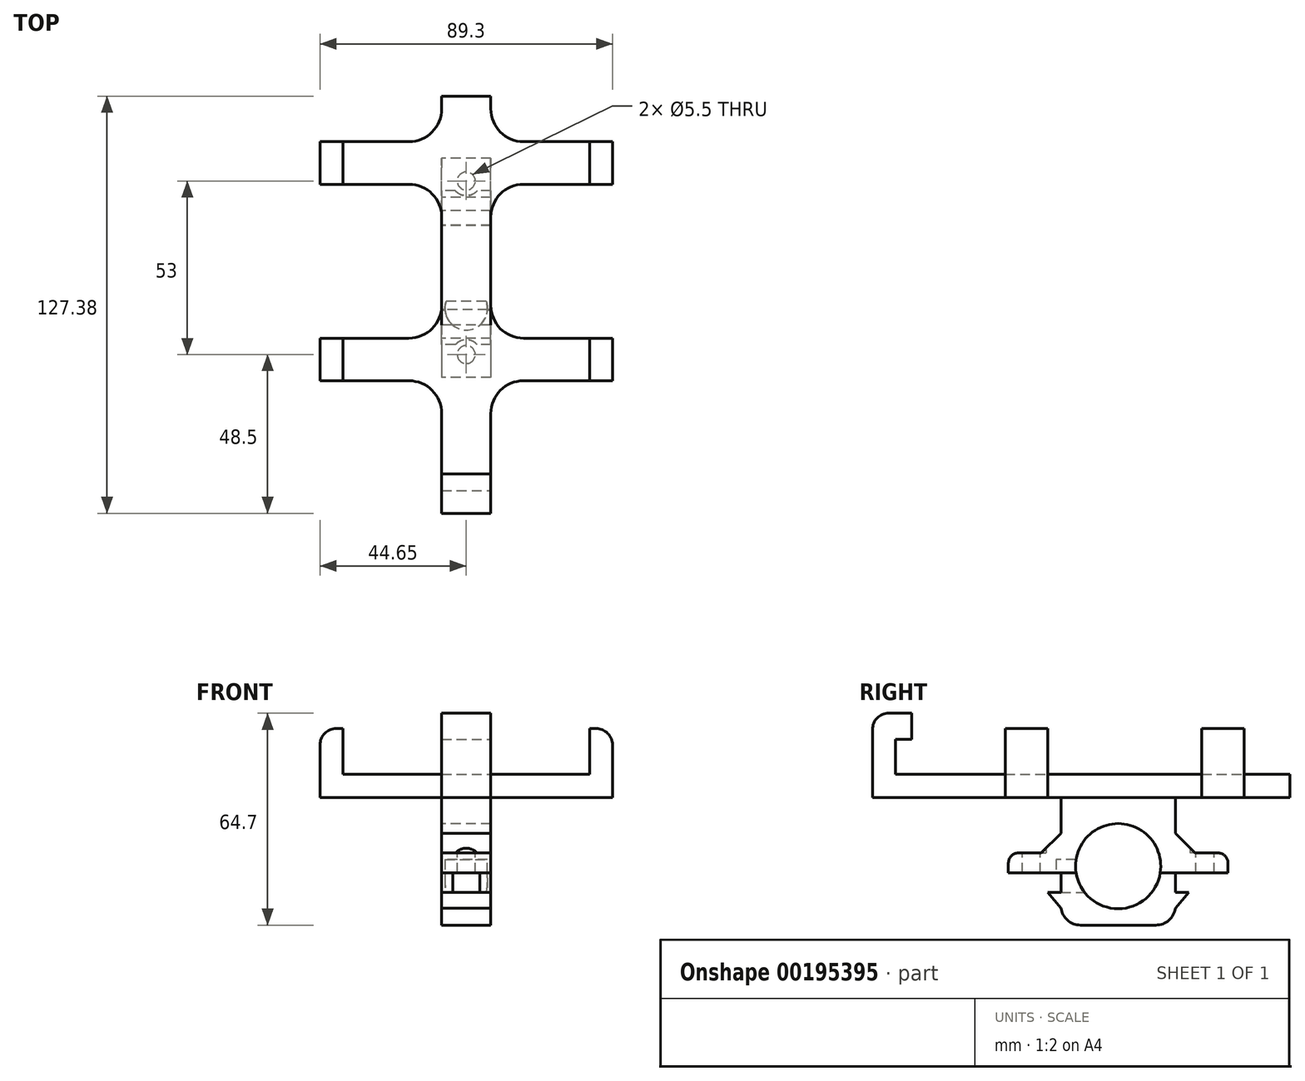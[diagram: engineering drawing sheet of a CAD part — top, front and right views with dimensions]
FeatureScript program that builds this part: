
annotation { "Feature Type Name" : "Feature", "Feature Type Description" : "" }
export const myFeature = defineFeature(function(context is Context, id is Id, definition is map)
    precondition{}
    {
        {
            var Q0;
            Q0=qCreatedBy(makeId("Top.planeOp"),FACE);
            var sketch = newSketch(context, id + "F0", { "sketchPlane" : qUnion([Q0])});
            skPoint(sketch, "E0.middle", {"position": v(0, 0) * mm});
            skPoint(sketch, "E1.middle", {"position": v(0, 25) * mm});
            skPoint(sketch, "E2.middle", {"position": v(0, -35) * mm});
            skLineSegment(sketch, "E3", {"start": v(-7.5, -75) * mm, "end": v(-7.5, 30) * mm});
            skLineSegment(sketch, "E4", {"start": v(7.5, 30) * mm, "end": v(7.5, -75) * mm});
            skLineSegment(sketch, "E5.top", {"start": v(-7.5, 45.38) * mm, "end": v(7.5, 45.38) * mm});
            skLineSegment(sketch, "E5.left", {"start": v(-7.5, 30) * mm, "end": v(-7.5, 45.38) * mm});
            skLineSegment(sketch, "E5.right", {"start": v(7.5, 30) * mm, "end": v(7.5, 45.38) * mm});
            skLineSegment(sketch, "E6.bottom", {"start": v(-37.65, -41.5) * mm, "end": v(37.65, -41.5) * mm});
            skLineSegment(sketch, "E6.top", {"start": v(-37.65, -28.5) * mm, "end": v(37.65, -28.5) * mm});
            skLineSegment(sketch, "E6.left", {"start": v(-37.65, -41.5) * mm, "end": v(-37.65, -28.5) * mm});
            skLineSegment(sketch, "E6.right", {"start": v(37.65, -41.5) * mm, "end": v(37.65, -28.5) * mm});
            skLineSegment(sketch, "E7", {"start": v(-7.5, -75) * mm, "end": v(7.5, -75) * mm});
            skLineSegment(sketch, "E8.bottom", {"start": v(37.65, 18.5) * mm, "end": v(-37.65, 18.5) * mm});
            skLineSegment(sketch, "E8.top", {"start": v(37.65, 31.5) * mm, "end": v(-37.65, 31.5) * mm});
            skLineSegment(sketch, "E8.left", {"start": v(37.65, 18.5) * mm, "end": v(37.65, 31.5) * mm});
            skLineSegment(sketch, "E8.right", {"start": v(-37.65, 18.5) * mm, "end": v(-37.65, 31.5) * mm});
            skLineSegment(sketch, "E9.bottom", {"start": v(-37.65, 31.5) * mm, "end": v(-44.65, 31.5) * mm});
            skLineSegment(sketch, "E9.top", {"start": v(-37.65, 18.5) * mm, "end": v(-44.65, 18.5) * mm});
            skLineSegment(sketch, "E9.left", {"start": v(-37.65, 31.5) * mm, "end": v(-37.65, 18.5) * mm});
            skLineSegment(sketch, "E9.right", {"start": v(-44.65, 31.5) * mm, "end": v(-44.65, 18.5) * mm});
            skLineSegment(sketch, "E10.bottom", {"start": v(-44.65, -28.5) * mm, "end": v(-37.65, -28.5) * mm});
            skLineSegment(sketch, "E10.top", {"start": v(-44.65, -41.5) * mm, "end": v(-37.65, -41.5) * mm});
            skLineSegment(sketch, "E10.left", {"start": v(-44.65, -28.5) * mm, "end": v(-44.65, -41.5) * mm});
            skLineSegment(sketch, "E10.right", {"start": v(-37.65, -28.5) * mm, "end": v(-37.65, -41.5) * mm});
            skLineSegment(sketch, "E11.bottom", {"start": v(37.65, 31.5) * mm, "end": v(44.65, 31.5) * mm});
            skLineSegment(sketch, "E11.top", {"start": v(37.65, 18.5) * mm, "end": v(44.65, 18.5) * mm});
            skLineSegment(sketch, "E11.left", {"start": v(37.65, 31.5) * mm, "end": v(37.65, 18.5) * mm});
            skLineSegment(sketch, "E11.right", {"start": v(44.65, 31.5) * mm, "end": v(44.65, 18.5) * mm});
            skLineSegment(sketch, "E12.bottom", {"start": v(44.65, -28.5) * mm, "end": v(37.65, -28.5) * mm});
            skLineSegment(sketch, "E12.top", {"start": v(44.65, -41.5) * mm, "end": v(37.65, -41.5) * mm});
            skLineSegment(sketch, "E12.left", {"start": v(44.65, -28.5) * mm, "end": v(44.65, -41.5) * mm});
            skLineSegment(sketch, "E12.right", {"start": v(37.65, -28.5) * mm, "end": v(37.65, -41.5) * mm});
            skLineSegment(sketch, "E13.top", {"start": v(-7.5, -82) * mm, "end": v(7.5, -82) * mm});
            skLineSegment(sketch, "E13.left", {"start": v(-7.5, -75) * mm, "end": v(-7.5, -82) * mm});
            skLineSegment(sketch, "E13.right", {"start": v(7.5, -75) * mm, "end": v(7.5, -82) * mm});
            skPoint(sketch, "E14", {"position": v(-17.5, 18.5) * mm});
            skPoint(sketch, "E15", {"position": v(-7.5, 8.5) * mm});
            skArc(sketch, "E16", {"start": v(-7.5, 8.5) * mm, "mid": v(-10.43, 15.57) * mm, "end": v(-17.5, 18.5) * mm});
            skPoint(sketch, "E17", {"position": v(-17.5, -28.5) * mm});
            skPoint(sketch, "E18", {"position": v(7.5, 8.5) * mm});
            skPoint(sketch, "E19", {"position": v(17.5, 18.5) * mm});
            skPoint(sketch, "E20", {"position": v(-7.5, -18.5) * mm});
            skPoint(sketch, "E21", {"position": v(7.5, -18.5) * mm});
            skPoint(sketch, "E22", {"position": v(17.5, -28.5) * mm});
            skPoint(sketch, "E23", {"position": v(17.5, -41.5) * mm});
            skPoint(sketch, "E24", {"position": v(7.5, -51.5) * mm});
            skPoint(sketch, "E25", {"position": v(-7.5, -51.5) * mm});
            skPoint(sketch, "E26", {"position": v(-17.5, -41.5) * mm});
            skPoint(sketch, "E27", {"position": v(17.5, 31.5) * mm});
            skPoint(sketch, "E28", {"position": v(7.5, 41.5) * mm});
            skPoint(sketch, "E29", {"position": v(-7.5, 41.5) * mm});
            skPoint(sketch, "E30", {"position": v(-17.5, 31.5) * mm});
            skArc(sketch, "E31", {"start": v(-17.5, 31.5) * mm, "mid": v(-10.43, 34.43) * mm, "end": v(-7.5, 41.5) * mm});
            skArc(sketch, "E32", {"start": v(7.5, 41.5) * mm, "mid": v(10.43, 34.43) * mm, "end": v(17.5, 31.5) * mm});
            skArc(sketch, "E33", {"start": v(17.5, 18.5) * mm, "mid": v(10.43, 15.57) * mm, "end": v(7.5, 8.5) * mm});
            skArc(sketch, "E34", {"start": v(7.5, -18.5) * mm, "mid": v(10.43, -25.57) * mm, "end": v(17.5, -28.5) * mm});
            skArc(sketch, "E35", {"start": v(17.5, -41.5) * mm, "mid": v(10.43, -44.43) * mm, "end": v(7.5, -51.5) * mm});
            skArc(sketch, "E36", {"start": v(-7.5, -51.5) * mm, "mid": v(-10.43, -44.43) * mm, "end": v(-17.5, -41.5) * mm});
            skArc(sketch, "E37", {"start": v(-17.5, -28.5) * mm, "mid": v(-10.43, -25.57) * mm, "end": v(-7.5, -18.5) * mm});
            skSolve(sketch);
        }
        {
            var Q0;
            Q0 = qSketchRegion(id + "F0", true);
            var Q1;
            {var subQ7=sQuery(id+"F0.wireOp",EDGE,"E5.left");var subQ8=sQuery(id+"F0.wireOp",EDGE,"E3");var subQ9=makeQuery(id+"F0.imprint","INTERSECT",VERTEX,{"derivedFrom":[subQ8,subQ7]});Q1=makeQuery(id+"F0.imprint","IMPRINT",FACE,{"disambiguationData":[TD([[makeQuery(id+"F0.imprint","IMPRINT",EDGE,{"disambiguationData":[TD([[subQ9,1.0]])],"derivedFrom":subQ8}),-1.0]])]});}
            var Q2;
            {var subQ0=sQuery(id+"F0.wireOp",EDGE,"E6.bottom");var subQ1=sQuery(id+"F0.wireOp",EDGE,"E3");var subQ2=makeQuery(id+"F0.imprint","INTERSECT",VERTEX,{"derivedFrom":[subQ1,subQ0]});Q2=makeQuery(id+"F0.imprint","IMPRINT",FACE,{"disambiguationData":[TD([[makeQuery(id+"F0.imprint","IMPRINT",EDGE,{"disambiguationData":[TD([[subQ2,-1.0]])],"derivedFrom":subQ1}),-1.0]])]});}
            extrude(context, id + "F1", {"entities" : qUnion([Q0, Q1, Q2]), "oppositeDirection" : true, "depth" : 7 * mm});
        }
        {
            var Q0;
            Q0=makeQuery(id+"F0.imprint","IMPRINT",FACE,{"disambiguationData":[TD([[makeQuery(id+"F0.imprint","IMPRINT",EDGE,{"derivedFrom":sQuery(id+"F0.wireOp",EDGE,"E9.bottom")}),1.0]])]});
            var Q1;
            Q1=makeQuery(id+"F0.imprint","IMPRINT",FACE,{"disambiguationData":[TD([[makeQuery(id+"F0.imprint","IMPRINT",EDGE,{"derivedFrom":sQuery(id+"F0.wireOp",EDGE,"E11.bottom")}),-1.0]])]});
            var Q2;
            Q2=makeQuery(id+"F0.imprint","IMPRINT",FACE,{"disambiguationData":[TD([[makeQuery(id+"F0.imprint","IMPRINT",EDGE,{"derivedFrom":sQuery(id+"F0.wireOp",EDGE,"E12.bottom")}),1.0]])]});
            var Q3;
            Q3=makeQuery(id+"F0.imprint","IMPRINT",FACE,{"disambiguationData":[TD([[makeQuery(id+"F0.imprint","IMPRINT",EDGE,{"derivedFrom":sQuery(id+"F0.wireOp",EDGE,"E10.bottom")}),-1.0]])]});
            extrude(context, id + "F2", {"entities" : qUnion([Q0, Q1, Q2, Q3]), "operationType" : NewBodyOperationType.ADD, "depth" : 14 * mm});
        }
        {
            var Q0;
            Q0=makeQuery(id+"F0.imprint","IMPRINT",FACE,{"disambiguationData":[TD([[makeQuery(id+"F0.imprint","IMPRINT",EDGE,{"derivedFrom":sQuery(id+"F0.wireOp",EDGE,"E7")}),-1.0]])]});
            extrude(context, id + "F3", {"entities" : qUnion([Q0]), "operationType" : NewBodyOperationType.ADD, "depth" : 10.7 * mm});
        }
        {
            var Q0;
            Q0=makeQuery(id+"F2.opExtrude","CAP_EDGE",EDGE,{"disambiguationData":[OSD([sQuery(id+"F0.wireOp",EDGE,"E9.right")])],"isStart":false});
            var Q1;
            Q1=makeQuery(id+"F2.opExtrude","CAP_EDGE",EDGE,{"disambiguationData":[OSD([sQuery(id+"F0.wireOp",EDGE,"E10.left")])],"isStart":false});
            var Q2;
            Q2=makeQuery(id+"F2.opExtrude","CAP_EDGE",EDGE,{"disambiguationData":[OSD([sQuery(id+"F0.wireOp",EDGE,"E12.left")])],"isStart":false});
            var Q3;
            Q3=makeQuery(id+"F2.opExtrude","CAP_EDGE",EDGE,{"disambiguationData":[OSD([sQuery(id+"F0.wireOp",EDGE,"E11.right")])],"isStart":false});
            fillet(context, id + "F4", {"entities" : qUnion([Q0, Q1, Q2, Q3]), "radius" : 5 * mm, "tangentPropagation" : true, "allowEdgeOverflow" : false});
        }
        {
            var Q0;
            Q0=makeQuery(id+"F3.opExtrude","CAP_FACE",FACE,{"disambiguationData":[OSD([sQuery(id+"F0.wireOp",EDGE,"E7"),sQuery(id+"F0.wireOp",EDGE,"E13.top"),sQuery(id+"F0.wireOp",EDGE,"E13.left"),sQuery(id+"F0.wireOp",EDGE,"E13.right")])],"isStart":false});
            extrude(context, id + "F5", {"entities" : qUnion([Q0]), "operationType" : NewBodyOperationType.ADD, "depth" : 8 * mm});
        }
        {
            var Q0;
            {var subQ0=sQuery(id+"F0.wireOp",EDGE,"E7");Q0=makeQuery(id+"F5.boolean.opBoolean","MERGE",FACE,{"derivedFrom":[makeQuery(id+"F3.opExtrude","SWEPT_FACE",FACE,{"disambiguationData":[OSD([subQ0])]}),makeQuery(id+"F5.opExtrude","SWEPT_FACE",FACE,{"disambiguationData":[OSD([subQ0])]})]});}
            var sketch = newSketch(context, id + "F6", { "sketchPlane" : qUnion([Q0])});
            skLineSegment(sketch, "E38.bottom", {"start": v(7.5, 18.7) * mm, "end": v(-7.5, 18.7) * mm});
            skLineSegment(sketch, "E38.top", {"start": v(7.5, 10.7) * mm, "end": v(-7.5, 10.7) * mm});
            skLineSegment(sketch, "E38.left", {"start": v(7.5, 18.7) * mm, "end": v(7.5, 10.7) * mm});
            skLineSegment(sketch, "E38.right", {"start": v(-7.5, 18.7) * mm, "end": v(-7.5, 10.7) * mm});
            skLineSegment(sketch, "E39", {"start": v(7.5, 0) * mm, "end": v(7.5, 10.7) * mm});
            skSolve(sketch);
        }
        {
            var Q0;
            Q0 = qSketchRegion(id + "F6", true);
            extrude(context, id + "F7", {"entities" : qUnion([Q0]), "operationType" : NewBodyOperationType.ADD, "depth" : 5 * mm});
        }
        {
            var Q0;
            Q0=makeQuery(id+"F5.opExtrude","CAP_EDGE",EDGE,{"disambiguationData":[OSD([sQuery(id+"F0.wireOp",EDGE,"E13.top")])],"isStart":false});
            fillet(context, id + "F8", {"entities" : qUnion([Q0]), "radius" : 5 * mm, "tangentPropagation" : true, "allowEdgeOverflow" : false});
        }
        {
            var Q0;
            Q0=qCreatedBy(makeId("Right.planeOp"),FACE);
            var sketch = newSketch(context, id + "F9", { "sketchPlane" : qUnion([Q0])});
            skLineSegment(sketch, "E40.top", {"start": v(10.5, -30) * mm, "end": v(-24.5, -30) * mm});
            skCircle(sketch, "E41", {"center": v(-7, -28) * mm, "radius": 13 * mm});
            skPoint(sketch, "E41.centerSnap0", {"position": v(-7, -30) * mm});
            skLineSegment(sketch, "E42.bottom", {"start": v(10.5, -30) * mm, "end": v(26.5, -30) * mm});
            skLineSegment(sketch, "E42.top", {"start": v(10.5, -24) * mm, "end": v(23.5, -24) * mm});
            skLineSegment(sketch, "E42.left", {"start": v(10.5, -30) * mm, "end": v(10.5, -24) * mm});
            skLineSegment(sketch, "E42.right", {"start": v(26.5, -30) * mm, "end": v(26.5, -27) * mm});
            skLineSegment(sketch, "E43.bottom", {"start": v(-24.5, -30) * mm, "end": v(-40.5, -30) * mm});
            skLineSegment(sketch, "E43.top", {"start": v(-24.5, -24) * mm, "end": v(-37.5, -24) * mm});
            skLineSegment(sketch, "E43.left", {"start": v(-24.5, -30) * mm, "end": v(-24.5, -24) * mm});
            skLineSegment(sketch, "E43.right", {"start": v(-40.5, -30) * mm, "end": v(-40.5, -27) * mm});
            skLineSegment(sketch, "E44.bottom", {"start": v(26.5, -30) * mm, "end": v(10.5, -30) * mm});
            skLineSegment(sketch, "E44.top", {"start": v(23.5, -36) * mm, "end": v(10.5, -36) * mm});
            skLineSegment(sketch, "E44.left", {"start": v(26.5, -30) * mm, "end": v(26.5, -33) * mm});
            skLineSegment(sketch, "E44.right", {"start": v(10.5, -30) * mm, "end": v(10.5, -36) * mm});
            skLineSegment(sketch, "E45.top", {"start": v(4.5, -46) * mm, "end": v(-18.5, -46) * mm});
            skLineSegment(sketch, "E45.left", {"start": v(10.5, -30) * mm, "end": v(10.5, -40) * mm});
            skLineSegment(sketch, "E45.right", {"start": v(-24.5, -30) * mm, "end": v(-24.5, -40) * mm});
            skLineSegment(sketch, "E46.bottom", {"start": v(-40.5, -30) * mm, "end": v(-24.5, -30) * mm});
            skLineSegment(sketch, "E46.top", {"start": v(-37.5, -36) * mm, "end": v(-24.5, -36) * mm});
            skLineSegment(sketch, "E46.left", {"start": v(-40.5, -30) * mm, "end": v(-40.5, -33) * mm});
            skLineSegment(sketch, "E46.right", {"start": v(-24.5, -30) * mm, "end": v(-24.5, -36) * mm});
            skPoint(sketch, "E47.visualSharp", {"position": v(10.5, -46) * mm});
            skArc(sketch, "E47.filletArc", {"start": v(4.5, -46) * mm, "mid": v(8.74, -44.24) * mm, "end": v(10.5, -40) * mm});
            skPoint(sketch, "E48.visualSharp", {"position": v(-24.5, -46) * mm});
            skArc(sketch, "E48.filletArc", {"start": v(-24.5, -40) * mm, "mid": v(-22.74, -44.24) * mm, "end": v(-18.5, -46) * mm});
            skLineSegment(sketch, "E49", {"start": v(16.5, -24) * mm, "end": v(10.5, -18) * mm});
            skLineSegment(sketch, "E50", {"start": v(-30.5, -24) * mm, "end": v(-24.5, -18) * mm});
            skPoint(sketch, "E51.visualSharp", {"position": v(26.5, -24) * mm});
            skArc(sketch, "E51.filletArc", {"start": v(26.5, -27) * mm, "mid": v(25.62, -24.88) * mm, "end": v(23.5, -24) * mm});
            skPoint(sketch, "E52.visualSharp", {"position": v(-40.5, -24) * mm});
            skArc(sketch, "E52.filletArc", {"start": v(-37.5, -24) * mm, "mid": v(-39.62, -24.88) * mm, "end": v(-40.5, -27) * mm});
            skPoint(sketch, "E53.visualSharp", {"position": v(-40.5, -36) * mm});
            skArc(sketch, "E53.filletArc", {"start": v(-40.5, -33) * mm, "mid": v(-39.62, -35.12) * mm, "end": v(-37.5, -36) * mm});
            skPoint(sketch, "E54.visualSharp", {"position": v(26.5, -36) * mm});
            skArc(sketch, "E54.filletArc", {"start": v(23.5, -36) * mm, "mid": v(25.62, -35.12) * mm, "end": v(26.5, -33) * mm});
            skLineSegment(sketch, "E55", {"start": v(-24.44, -40.84) * mm, "end": v(-28.5, -36) * mm});
            skLineSegment(sketch, "E56", {"start": v(10.44, -40.84) * mm, "end": v(14.5, -36) * mm});
            skPoint(sketch, "E57", {"position": v(0, -7) * mm});
            skLineSegment(sketch, "E58", {"start": v(10.5, -7) * mm, "end": v(-24.5, -7) * mm});
            skLineSegment(sketch, "E59", {"start": v(10.5, -7) * mm, "end": v(10.5, -24) * mm});
            skLineSegment(sketch, "E60", {"start": v(-24.5, -7) * mm, "end": v(-24.5, -24) * mm});
            skSolve(sketch);
        }
        {
            var Q0;
            Q0=makeQuery(id+"F9.imprint","IMPRINT",FACE,{"disambiguationData":[TD([[makeQuery(id+"F9.imprint","IMPRINT",EDGE,{"derivedFrom":sQuery(id+"F9.wireOp",EDGE,"E42.top")}),-1.0]])]});
            var Q1;
            Q1=makeQuery(id+"F9.imprint","IMPRINT",FACE,{"disambiguationData":[TD([[makeQuery(id+"F9.imprint","IMPRINT",EDGE,{"derivedFrom":sQuery(id+"F9.wireOp",EDGE,"E40.bottom")}),1.0]])]});
            var Q2;
            Q2=makeQuery(id+"F9.imprint","IMPRINT",FACE,{"disambiguationData":[TD([[makeQuery(id+"F9.imprint","IMPRINT",EDGE,{"derivedFrom":sQuery(id+"F9.wireOp",EDGE,"E43.top")}),1.0]])]});
            var Q3;
            {var subQ3=sQuery(id+"F9.wireOp",EDGE,"E49");Q3=makeQuery(id+"F9.imprint","IMPRINT",FACE,{"disambiguationData":[TD([[makeQuery(id+"F9.imprint","IMPRINT",EDGE,{"derivedFrom":subQ3}),1.0]])]});}
            var Q4;
            {var subQ3=sQuery(id+"F9.wireOp",EDGE,"E50");Q4=makeQuery(id+"F9.imprint","IMPRINT",FACE,{"disambiguationData":[TD([[makeQuery(id+"F9.imprint","IMPRINT",EDGE,{"derivedFrom":subQ3}),-1.0]])]});}
            var Q5;
            {var subQ1=sQuery(id+"F9.wireOp",EDGE,"E42.left");Q5=makeQuery(id+"F9.imprint","IMPRINT",FACE,{"disambiguationData":[TD([[makeQuery(id+"F9.imprint","IMPRINT",EDGE,{"derivedFrom":subQ1}),1.0]])]});}
            extrude(context, id + "F10", {"entities" : qUnion([Q0, Q1, Q2, Q3, Q4, Q5]), "endBound" : BoundingType.SYMMETRIC, "depth" : 15 * mm});
        }
        {
            var Q0;
            {var subQ2=sQuery(id+"F9.wireOp",EDGE,"E44.bottom");Q0=makeQuery(id+"F9.imprint","IMPRINT",FACE,{"disambiguationData":[TD([[makeQuery(id+"F9.imprint","IMPRINT",EDGE,{"derivedFrom":subQ2}),1.0]])]});}
            var Q1;
            Q1=makeQuery(id+"F9.imprint","IMPRINT",FACE,{"disambiguationData":[TD([[makeQuery(id+"F9.imprint","IMPRINT",EDGE,{"derivedFrom":sQuery(id+"F9.wireOp",EDGE,"E45.top")}),-1.0]])]});
            var Q2;
            Q2=makeQuery(id+"F9.imprint","IMPRINT",FACE,{"disambiguationData":[TD([[makeQuery(id+"F9.imprint","IMPRINT",EDGE,{"derivedFrom":sQuery(id+"F9.wireOp",EDGE,"E46.bottom")}),-1.0]])]});
            var Q3;
            {var subQ0=sQuery(id+"F9.wireOp",EDGE,"E45.right");Q3=makeQuery(id+"F9.imprint","IMPRINT",FACE,{"disambiguationData":[TD([[makeQuery(id+"F9.imprint","IMPRINT",EDGE,{"derivedFrom":subQ0}),-1.0]])]});}
            var Q4;
            {var subQ3=sQuery(id+"F9.wireOp",EDGE,"Dz0G4xqv-ALU2-ZbiM-SCfw-WAiNGFc8qngV");Q4=makeQuery(id+"F9.imprint","IMPRINT",FACE,{"disambiguationData":[TD([[makeQuery(id+"F9.imprint","IMPRINT",EDGE,{"derivedFrom":subQ3}),1.0]])]});}
            var Q5;
            {var subQ3=sQuery(id+"F9.wireOp",EDGE,"E56");Q5=makeQuery(id+"F9.imprint","IMPRINT",FACE,{"disambiguationData":[TD([[makeQuery(id+"F9.imprint","IMPRINT",EDGE,{"derivedFrom":subQ3}),1.0]])]});}
            extrude(context, id + "F11", {"entities" : qUnion([Q0, Q1, Q2, Q3, Q4, Q5]), "endBound" : BoundingType.SYMMETRIC, "depth" : 15 * mm});
        }
        {
            var Q0;
            Q0=makeQuery(id+"F10.opExtrude","SWEPT_FACE",FACE,{"disambiguationData":[OSD([sQuery(id+"F9.wireOp",EDGE,"E43.top")])]});
            var sketch = newSketch(context, id + "F12", { "sketchPlane" : qUnion([Q0])});
            skCircle(sketch, "E61", {"center": v(0, -33.5) * mm, "radius": 2.75 * mm});
            skPoint(sketch, "E61.centerSnap0", {"position": v(0, -37.5) * mm});
            skCircle(sketch, "E62", {"center": v(0, -33.5) * mm, "radius": 4.5 * mm});
            skSolve(sketch);
        }
        {
            var Q0;
            Q0=makeQuery(id+"F12.imprint","IMPRINT",FACE,{"disambiguationData":[TD([[makeQuery(id+"F12.imprint","IMPRINT",EDGE,{"derivedFrom":sQuery(id+"F12.wireOp",EDGE,"E61")}),1.0]])]});
            extrude(context, id + "F13", {"entities" : qUnion([Q0]), "operationType" : NewBodyOperationType.REMOVE, "endBound" : BoundingType.THROUGH_ALL, "oppositeDirection" : true, "depth" : 25 * mm});
        }
        {
            var Q0;
            Q0=makeQuery(id+"F12.imprint","IMPRINT",FACE,{"disambiguationData":[TD([[makeQuery(id+"F12.imprint","IMPRINT",EDGE,{"derivedFrom":sQuery(id+"F12.wireOp",EDGE,"E61")}),-1.0]])]});
            var Q1;
            {var subQ0=sQuery(id+"F12.wireOp",EDGE,"E62");var subQ1=makeQuery(id+"F10.opExtrude","SWEPT_EDGE",EDGE,{"disambiguationData":[OSD([sQuery(id+"F9.wireOp",EDGE,"E43.top"),sQuery(id+"F9.wireOp",EDGE,"E52.filletArc")])]});var subQ2=makeQuery(id+"F12.imprint","INTERSECT",VERTEX,{"disambiguationData":[OD(0.0)],"derivedFrom":[subQ1,subQ0]});Q1=makeQuery(id+"F12.imprint","IMPRINT",FACE,{"disambiguationData":[TD([[makeQuery(id+"F12.imprint","IMPRINT",EDGE,{"disambiguationData":[TD([[subQ2,-1.0]])],"derivedFrom":subQ0}),1.0]])]});}
            var Q2;
            {var subQ0=sQuery(id+"F12.wireOp",EDGE,"E62");var subQ1=makeQuery(id+"F10.opExtrude","SWEPT_EDGE",EDGE,{"disambiguationData":[OSD([sQuery(id+"F9.wireOp",EDGE,"E43.top"),sQuery(id+"F9.wireOp",EDGE,"E50")])]});var subQ2=makeQuery(id+"F12.imprint","INTERSECT",VERTEX,{"disambiguationData":[OD(0.0)],"derivedFrom":[subQ1,subQ0]});Q2=makeQuery(id+"F12.imprint","IMPRINT",FACE,{"disambiguationData":[TD([[makeQuery(id+"F12.imprint","IMPRINT",EDGE,{"disambiguationData":[TD([[subQ2,1.0]])],"derivedFrom":subQ0}),1.0]])]});}
            extrude(context, id + "F14", {"entities" : qUnion([Q0, Q1, Q2]), "operationType" : NewBodyOperationType.REMOVE, "depth" : 10 * mm});
        }
        {
            var Q0;
            Q0=makeQuery(id+"F10.opExtrude","SWEPT_FACE",FACE,{"disambiguationData":[OSD([sQuery(id+"F9.wireOp",EDGE,"E42.top")])]});
            var sketch = newSketch(context, id + "F15", { "sketchPlane" : qUnion([Q0])});
            skCircle(sketch, "E63", {"center": v(0, 19.5) * mm, "radius": 2.75 * mm});
            skPoint(sketch, "E63.centerSnap0", {"position": v(0, 23.5) * mm});
            skCircle(sketch, "E64", {"center": v(0, 19.5) * mm, "radius": 4.5 * mm});
            skSolve(sketch);
        }
        {
            var Q0;
            Q0=makeQuery(id+"F15.imprint","IMPRINT",FACE,{"disambiguationData":[TD([[makeQuery(id+"F15.imprint","IMPRINT",EDGE,{"derivedFrom":sQuery(id+"F15.wireOp",EDGE,"E63")}),1.0]])]});
            extrude(context, id + "F16", {"entities" : qUnion([Q0]), "operationType" : NewBodyOperationType.REMOVE, "endBound" : BoundingType.THROUGH_ALL, "oppositeDirection" : true, "depth" : 25 * mm});
        }
        {
            var Q0;
            Q0=makeQuery(id+"F15.imprint","IMPRINT",FACE,{"disambiguationData":[TD([[makeQuery(id+"F15.imprint","IMPRINT",EDGE,{"derivedFrom":sQuery(id+"F15.wireOp",EDGE,"E63")}),-1.0]])]});
            var Q1;
            {var subQ0=sQuery(id+"F15.wireOp",EDGE,"E64");var subQ1=makeQuery(id+"F10.opExtrude","SWEPT_EDGE",EDGE,{"disambiguationData":[OSD([sQuery(id+"F9.wireOp",EDGE,"E42.top"),sQuery(id+"F9.wireOp",EDGE,"E49")])]});var subQ2=makeQuery(id+"F15.imprint","INTERSECT",VERTEX,{"disambiguationData":[OD(0.0)],"derivedFrom":[subQ1,subQ0]});Q1=makeQuery(id+"F15.imprint","IMPRINT",FACE,{"disambiguationData":[TD([[makeQuery(id+"F15.imprint","IMPRINT",EDGE,{"disambiguationData":[TD([[subQ2,-1.0]])],"derivedFrom":subQ0}),1.0]])]});}
            var Q2;
            {var subQ0=sQuery(id+"F15.wireOp",EDGE,"E64");var subQ1=makeQuery(id+"F10.opExtrude","SWEPT_EDGE",EDGE,{"disambiguationData":[OSD([sQuery(id+"F9.wireOp",EDGE,"E42.top"),sQuery(id+"F9.wireOp",EDGE,"E51.filletArc")])]});var subQ2=makeQuery(id+"F15.imprint","INTERSECT",VERTEX,{"disambiguationData":[OD(0.0)],"derivedFrom":[subQ1,subQ0]});Q2=makeQuery(id+"F15.imprint","IMPRINT",FACE,{"disambiguationData":[TD([[makeQuery(id+"F15.imprint","IMPRINT",EDGE,{"disambiguationData":[TD([[subQ2,1.0]])],"derivedFrom":subQ0}),1.0]])]});}
            extrude(context, id + "F17", {"entities" : qUnion([Q0, Q1, Q2]), "operationType" : NewBodyOperationType.REMOVE, "depth" : 10 * mm});
        }
        {
            var Q0;
            Q0=makeQuery(id+"F11.opExtrude","SWEPT_FACE",FACE,{"disambiguationData":[OSD([sQuery(id+"F9.wireOp",EDGE,"E44.top")])]});
            var sketch = newSketch(context, id + "F18", { "sketchPlane" : qUnion([Q0])});
            skCircle(sketch, "E65", {"center": v(0, -19.5) * mm, "radius": 6.5 * mm});
            skSolve(sketch);
        }
        {
            var Q0;
            Q0=makeQuery(id+"F11.opExtrude","SWEPT_FACE",FACE,{"disambiguationData":[OSD([sQuery(id+"F9.wireOp",EDGE,"E46.top")])]});
            var sketch = newSketch(context, id + "F19", { "sketchPlane" : qUnion([Q0])});
            skCircle(sketch, "E66", {"center": v(0, 33.5) * mm, "radius": 6.5 * mm});
            skSolve(sketch);
        }
        {
            var Q0;
            {var subQ0=sQuery(id+"F19.wireOp",EDGE,"E66");var subQ1=makeQuery(id+"F11.opExtrude","SWEPT_EDGE",EDGE,{"disambiguationData":[OSD([sQuery(id+"F9.wireOp",EDGE,"E46.top"),sQuery(id+"F9.wireOp",EDGE,"E53.filletArc")])]});var subQ2=makeQuery(id+"F19.imprint","INTERSECT",VERTEX,{"disambiguationData":[OD(0.0)],"derivedFrom":[subQ1,subQ0]});Q0=makeQuery(id+"F19.imprint","IMPRINT",FACE,{"disambiguationData":[TD([[makeQuery(id+"F19.imprint","IMPRINT",EDGE,{"disambiguationData":[TD([[subQ2,1.0]])],"derivedFrom":subQ0}),1.0]])]});}
            var Q1;
            {var subQ0=sQuery(id+"F19.wireOp",EDGE,"E66");var subQ1=makeQuery(id+"F11.opExtrude","SWEPT_EDGE",EDGE,{"disambiguationData":[OSD([sQuery(id+"F9.wireOp",EDGE,"E46.top"),sQuery(id+"F9.wireOp",EDGE,"E55")])]});var subQ2=makeQuery(id+"F19.imprint","INTERSECT",VERTEX,{"disambiguationData":[OD(0.0)],"derivedFrom":[subQ1,subQ0]});Q1=makeQuery(id+"F19.imprint","IMPRINT",FACE,{"disambiguationData":[TD([[makeQuery(id+"F19.imprint","IMPRINT",EDGE,{"disambiguationData":[TD([[subQ2,-1.0]])],"derivedFrom":subQ0}),1.0]])]});}
            var Q2;
            {var subQ1=sQuery(id+"F9.wireOp",EDGE,"E46.top");Q2=makeQuery(id+"F19.imprint","IMPRINT",FACE,{"disambiguationData":[TD([[makeQuery(id+"F19.imprint","IMPRINT",EDGE,{"derivedFrom":makeQuery(id+"F13.boolean.opBoolean","INTERSECT",EDGE,{"derivedFrom":[makeQuery(id+"F11.opExtrude","SWEPT_FACE",FACE,{"disambiguationData":[OSD([subQ1])]}),makeQuery(id+"F13.opExtrude","SWEPT_FACE",FACE,{"disambiguationData":[OSD([sQuery(id+"F12.wireOp",EDGE,"E61")])]})]})}),1.0]])]});}
            extrude(context, id + "F20", {"entities" : qUnion([Q0, Q1, Q2]), "operationType" : NewBodyOperationType.REMOVE, "depth" : 10 * mm});
        }
        {
            var Q0;
            Q0 = qSketchRegion(id + "F18", true);
            extrude(context, id + "F21", {"entities" : qUnion([Q0]), "operationType" : NewBodyOperationType.REMOVE, "depth" : 10 * mm});
        }
    });
